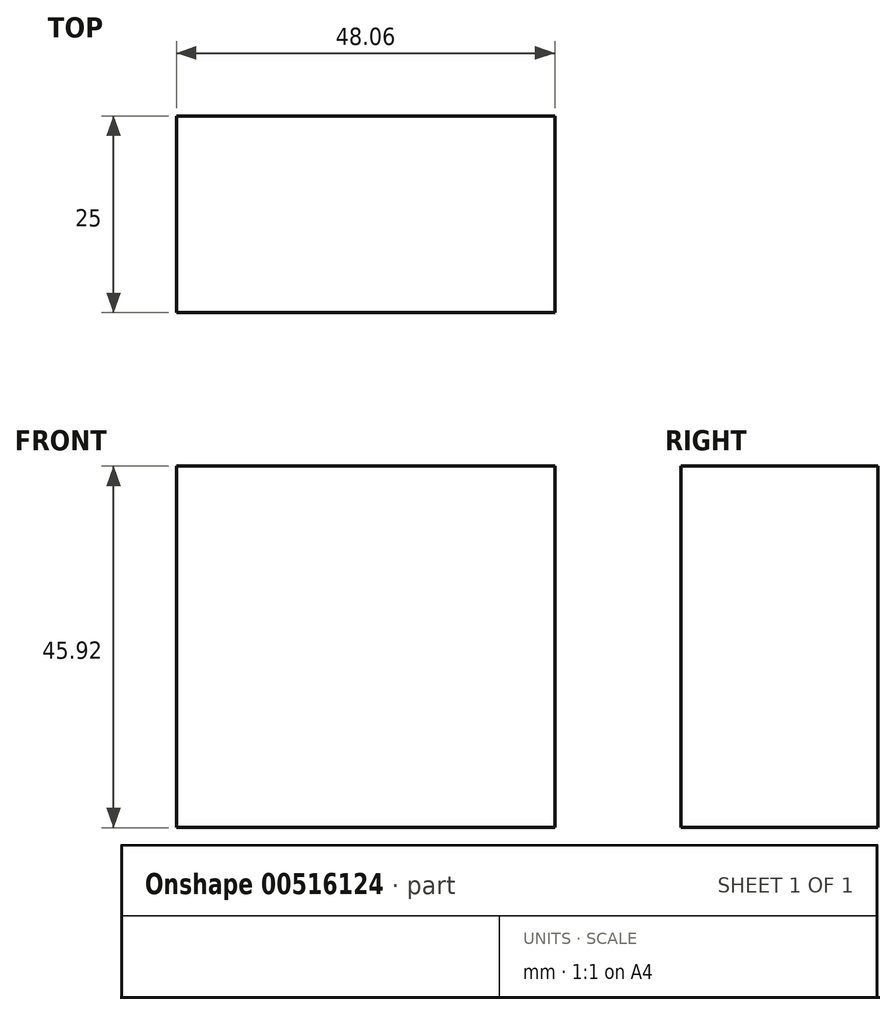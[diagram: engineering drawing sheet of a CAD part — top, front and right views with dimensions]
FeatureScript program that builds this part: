
annotation { "Feature Type Name" : "Feature", "Feature Type Description" : "" }
export const myFeature = defineFeature(function(context is Context, id is Id, definition is map)
    precondition{}
    {
        {
            var Q0;
            Q0=qCreatedBy(makeId("Front.planeOp"),FACE);
            var sketch = newSketch(context, id + "F0", { "sketchPlane" : qUnion([Q0])});
            skLineSegment(sketch, "E0.bottom", {"start": v(-118.5, -21.86) * mm, "end": v(-70.43, -21.86) * mm});
            skLineSegment(sketch, "E0.top", {"start": v(-118.5, 24.06) * mm, "end": v(-70.43, 24.06) * mm});
            skLineSegment(sketch, "E0.left", {"start": v(-118.5, -21.86) * mm, "end": v(-118.5, 24.06) * mm});
            skLineSegment(sketch, "E0.right", {"start": v(-70.43, -21.86) * mm, "end": v(-70.43, 24.06) * mm});
            skPoint(sketch, "E0.middle", {"position": v(-94.46, 1.1) * mm});
            skSolve(sketch);
        }
        {
            var Q0;
            Q0=makeQuery(id+"F0.imprint","IMPRINT",FACE,{"disambiguationData":[TD([[makeQuery(id+"F0.imprint","IMPRINT",EDGE,{"derivedFrom":sQuery(id+"F0.wireOp",EDGE,"E0.bottom")}),1.0]])]});
            extrude(context, id + "F1", {"entities" : qUnion([Q0]), "depth" : 25 * mm, "offsetDistance" : 25 * mm});
        }
    });
